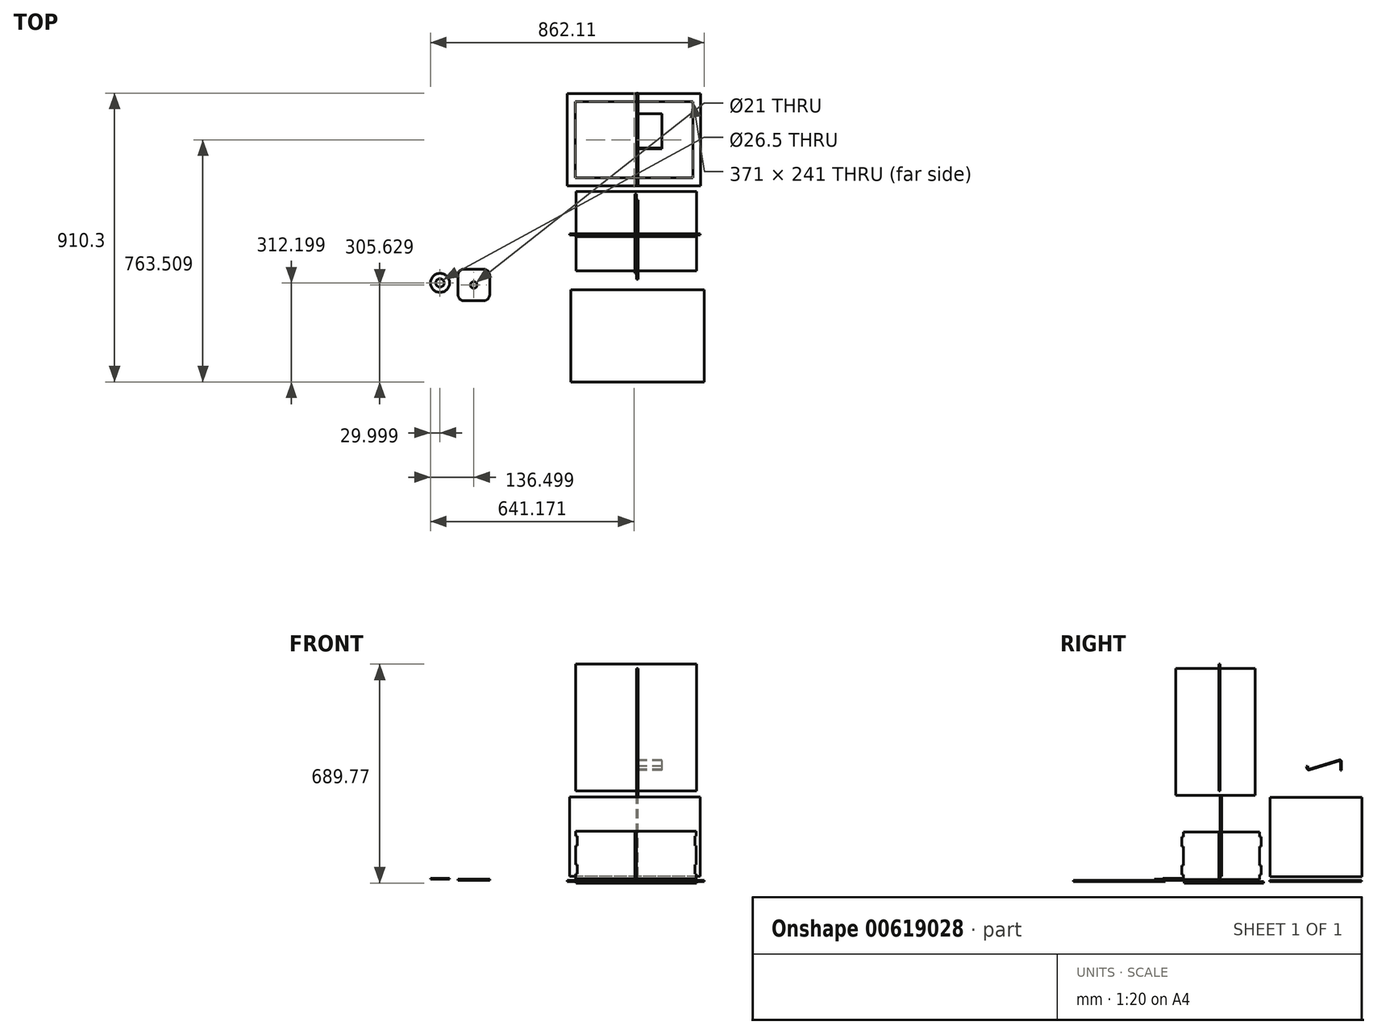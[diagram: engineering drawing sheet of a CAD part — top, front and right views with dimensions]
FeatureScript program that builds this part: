
annotation { "Feature Type Name" : "Feature", "Feature Type Description" : "" }
export const myFeature = defineFeature(function(context is Context, id is Id, definition is map)
    precondition{}
    {
        {
            var Q0;
            Q0=qCreatedBy(makeId("Top.planeOp"),FACE);
            var sketch = newSketch(context, id + "F0", { "sketchPlane" : qUnion([Q0])});
            skLineSegment(sketch, "E0.bottom", {"start": v(-185.88, 137.35) * mm, "end": v(194.12, 137.35) * mm});
            skLineSegment(sketch, "E0.top", {"start": v(-185.88, -112.65) * mm, "end": v(194.12, -112.65) * mm});
            skLineSegment(sketch, "E0.left", {"start": v(-185.88, 137.35) * mm, "end": v(-185.88, -112.65) * mm});
            skLineSegment(sketch, "E0.right", {"start": v(194.12, 137.35) * mm, "end": v(194.12, -112.65) * mm});
            skSolve(sketch);
        }
        {
            var Q0;
            Q0 = qSketchRegion(id + "F0", true);
            extrude(context, id + "F1", {"entities" : qUnion([Q0]), "depth" : 4.5 * mm, "offsetDistance" : 25 * mm});
        }
        {
            var Q0;
            Q0=qCreatedBy(makeId("Front.planeOp"),FACE);
            var sketch = newSketch(context, id + "F2", { "sketchPlane" : qUnion([Q0])});
            skLineSegment(sketch, "E1.bottom", {"start": v(-187.27, 13.24) * mm, "end": v(192.73, 13.24) * mm});
            skLineSegment(sketch, "E1.top", {"start": v(-187.27, 163.24) * mm, "end": v(192.73, 163.24) * mm});
            skLineSegment(sketch, "E1.left", {"start": v(-187.27, 13.24) * mm, "end": v(-187.27, 28.24) * mm});
            skLineSegment(sketch, "E1.right", {"start": v(192.73, 13.24) * mm, "end": v(192.73, 28.24) * mm});
            skLineSegment(sketch, "E2", {"start": v(-187.27, 148.24) * mm, "end": v(-182.77, 148.24) * mm});
            skLineSegment(sketch, "E3", {"start": v(-182.77, 148.24) * mm, "end": v(-182.77, 118.24) * mm});
            skLineSegment(sketch, "E4", {"start": v(-182.77, 118.24) * mm, "end": v(-187.27, 118.24) * mm});
            skLineSegment(sketch, "E5", {"start": v(-187.27, 58.24) * mm, "end": v(-182.77, 58.24) * mm});
            skLineSegment(sketch, "E6", {"start": v(-182.77, 58.24) * mm, "end": v(-182.77, 28.24) * mm});
            skLineSegment(sketch, "E7", {"start": v(-182.77, 28.24) * mm, "end": v(-187.27, 28.24) * mm});
            skLineSegment(sketch, "E8.trimOffspring", {"start": v(-187.27, 148.24) * mm, "end": v(-187.27, 163.24) * mm});
            skLineSegment(sketch, "E9.trimOffspring", {"start": v(-187.27, 58.24) * mm, "end": v(-187.27, 118.24) * mm});
            skLineSegment(sketch, "E10", {"start": v(192.73, 148.24) * mm, "end": v(188.23, 148.24) * mm});
            skLineSegment(sketch, "E11", {"start": v(188.23, 148.24) * mm, "end": v(188.23, 118.24) * mm});
            skLineSegment(sketch, "E12", {"start": v(188.23, 118.24) * mm, "end": v(192.73, 118.24) * mm});
            skLineSegment(sketch, "E13", {"start": v(192.73, 58.24) * mm, "end": v(188.23, 58.24) * mm});
            skLineSegment(sketch, "E14", {"start": v(188.23, 58.24) * mm, "end": v(188.23, 28.24) * mm});
            skLineSegment(sketch, "E15", {"start": v(188.23, 28.24) * mm, "end": v(192.73, 28.24) * mm});
            skLineSegment(sketch, "E16.trimOffspring", {"start": v(192.73, 148.24) * mm, "end": v(192.73, 163.24) * mm});
            skLineSegment(sketch, "E17.trimOffspring", {"start": v(192.73, 58.24) * mm, "end": v(192.73, 118.24) * mm});
            skSolve(sketch);
        }
        {
            var Q0;
            Q0 = qSketchRegion(id + "F2", true);
            extrude(context, id + "F3", {"entities" : qUnion([Q0]), "depth" : 4.5 * mm, "offsetDistance" : 25 * mm});
        }
        {
            var Q0;
            Q0=qCreatedBy(makeId("Right.planeOp"),FACE);
            var sketch = newSketch(context, id + "F4", { "sketchPlane" : qUnion([Q0])});
            skLineSegment(sketch, "E18.bottom", {"start": v(-116.2, 10.64) * mm, "end": v(124.8, 10.64) * mm});
            skLineSegment(sketch, "E18.top", {"start": v(-116.2, 160.64) * mm, "end": v(124.8, 160.64) * mm});
            skLineSegment(sketch, "E18.left", {"start": v(-116.2, 10.64) * mm, "end": v(-116.2, 25.64) * mm});
            skLineSegment(sketch, "E18.right", {"start": v(124.8, 10.64) * mm, "end": v(124.8, 25.64) * mm});
            skLineSegment(sketch, "E19", {"start": v(-116.2, 145.64) * mm, "end": v(-120.7, 145.64) * mm});
            skLineSegment(sketch, "E20", {"start": v(-120.7, 145.64) * mm, "end": v(-120.7, 115.64) * mm});
            skLineSegment(sketch, "E21", {"start": v(-120.7, 115.64) * mm, "end": v(-116.2, 115.64) * mm});
            skLineSegment(sketch, "E22", {"start": v(-116.2, 55.64) * mm, "end": v(-120.7, 55.64) * mm});
            skLineSegment(sketch, "E23", {"start": v(-120.7, 55.64) * mm, "end": v(-120.7, 25.64) * mm});
            skLineSegment(sketch, "E24", {"start": v(-120.7, 25.64) * mm, "end": v(-116.2, 25.64) * mm});
            skLineSegment(sketch, "E25.trimOffspring", {"start": v(-116.2, 145.64) * mm, "end": v(-116.2, 160.64) * mm});
            skLineSegment(sketch, "E26.trimOffspring", {"start": v(-116.2, 55.64) * mm, "end": v(-116.2, 115.64) * mm});
            skLineSegment(sketch, "E27", {"start": v(124.8, 145.64) * mm, "end": v(129.3, 145.64) * mm});
            skLineSegment(sketch, "E28", {"start": v(129.3, 145.64) * mm, "end": v(129.3, 115.64) * mm});
            skLineSegment(sketch, "E29", {"start": v(129.3, 115.64) * mm, "end": v(124.8, 115.64) * mm});
            skLineSegment(sketch, "E30", {"start": v(124.8, 55.64) * mm, "end": v(129.3, 55.64) * mm});
            skLineSegment(sketch, "E31", {"start": v(129.3, 55.64) * mm, "end": v(129.3, 25.64) * mm});
            skLineSegment(sketch, "E32", {"start": v(129.3, 25.64) * mm, "end": v(124.8, 25.64) * mm});
            skLineSegment(sketch, "E33.trimOffspring", {"start": v(124.8, 145.64) * mm, "end": v(124.8, 160.64) * mm});
            skLineSegment(sketch, "E34.trimOffspring", {"start": v(124.8, 55.64) * mm, "end": v(124.8, 115.64) * mm});
            skSolve(sketch);
        }
        {
            var Q0;
            Q0 = qSketchRegion(id + "F4", true);
            extrude(context, id + "F5", {"entities" : qUnion([Q0]), "depth" : 4.5 * mm, "offsetDistance" : 25 * mm});
        }
        {
            var Q0;
            Q0=makeQuery(id+"F1.opExtrude","CAP_FACE",FACE,{"disambiguationData":[OSD([sQuery(id+"F0.wireOp",EDGE,"E0.bottom"),sQuery(id+"F0.wireOp",EDGE,"E0.top"),sQuery(id+"F0.wireOp",EDGE,"E0.left"),sQuery(id+"F0.wireOp",EDGE,"E0.right")])],"isStart":false});
            var sketch = newSketch(context, id + "F6", { "sketchPlane" : qUnion([Q0])});
            skLineSegment(sketch, "E35.bottom", {"start": v(-189.13, 179.9) * mm, "end": v(181.87, 179.9) * mm});
            skLineSegment(sketch, "E35.top", {"start": v(-189.13, 420.9) * mm, "end": v(181.87, 420.9) * mm});
            skLineSegment(sketch, "E35.left", {"start": v(-189.13, 179.9) * mm, "end": v(-189.13, 420.9) * mm});
            skLineSegment(sketch, "E35.right", {"start": v(181.87, 179.9) * mm, "end": v(181.87, 420.9) * mm});
            skLineSegment(sketch, "E36.bottom", {"start": v(-213.63, 155.4) * mm, "end": v(206.37, 155.4) * mm});
            skLineSegment(sketch, "E36.top", {"start": v(-213.63, 445.4) * mm, "end": v(206.37, 445.4) * mm});
            skLineSegment(sketch, "E36.left", {"start": v(-213.63, 155.4) * mm, "end": v(-213.63, 445.4) * mm});
            skLineSegment(sketch, "E36.right", {"start": v(206.37, 155.4) * mm, "end": v(206.37, 445.4) * mm});
            skSolve(sketch);
        }
        {
            var Q0;
            Q0 = qSketchRegion(id + "F6", true);
            extrude(context, id + "F7", {"entities" : qUnion([Q0]), "depth" : 4.5 * mm, "offsetDistance" : 25 * mm});
        }
        {
            var Q0;
            Q0=makeQuery(id+"F5.opExtrude","CAP_FACE",FACE,{"disambiguationData":[OSD([sQuery(id+"F4.wireOp",EDGE,"E18.bottom"),sQuery(id+"F4.wireOp",EDGE,"E18.top"),sQuery(id+"F4.wireOp",EDGE,"E18.left"),sQuery(id+"F4.wireOp",EDGE,"E18.right"),sQuery(id+"F4.wireOp",EDGE,"E19"),sQuery(id+"F4.wireOp",EDGE,"E20"),sQuery(id+"F4.wireOp",EDGE,"E21"),sQuery(id+"F4.wireOp",EDGE,"E22"),sQuery(id+"F4.wireOp",EDGE,"E23"),sQuery(id+"F4.wireOp",EDGE,"E24"),sQuery(id+"F4.wireOp",EDGE,"E25.trimOffspring"),sQuery(id+"F4.wireOp",EDGE,"E26.trimOffspring"),sQuery(id+"F4.wireOp",EDGE,"E27"),sQuery(id+"F4.wireOp",EDGE,"E28"),sQuery(id+"F4.wireOp",EDGE,"E29"),sQuery(id+"F4.wireOp",EDGE,"E30"),sQuery(id+"F4.wireOp",EDGE,"E31"),sQuery(id+"F4.wireOp",EDGE,"E32"),sQuery(id+"F4.wireOp",EDGE,"E33.trimOffspring"),sQuery(id+"F4.wireOp",EDGE,"E34.trimOffspring")])],"isStart":false});
            var sketch = newSketch(context, id + "F8", { "sketchPlane" : qUnion([Q0])});
            skLineSegment(sketch, "E37.bottom", {"start": v(157.19, 19.82) * mm, "end": v(447.19, 19.82) * mm});
            skLineSegment(sketch, "E37.top", {"start": v(157.19, 269.82) * mm, "end": v(447.19, 269.82) * mm});
            skLineSegment(sketch, "E37.left", {"start": v(157.19, 19.82) * mm, "end": v(157.19, 269.82) * mm});
            skLineSegment(sketch, "E37.right", {"start": v(447.19, 19.82) * mm, "end": v(447.19, 269.82) * mm});
            skSolve(sketch);
        }
        {
            var Q0;
            Q0 = qSketchRegion(id + "F8", true);
            extrude(context, id + "F9", {"entities" : qUnion([Q0]), "depth" : 4.5 * mm, "offsetDistance" : 25 * mm});
        }
        {
            var Q0;
            Q0=makeQuery(id+"F3.opExtrude","CAP_FACE",FACE,{"disambiguationData":[OSD([sQuery(id+"F2.wireOp",EDGE,"E1.bottom"),sQuery(id+"F2.wireOp",EDGE,"E1.top"),sQuery(id+"F2.wireOp",EDGE,"E1.left"),sQuery(id+"F2.wireOp",EDGE,"E1.right"),sQuery(id+"F2.wireOp",EDGE,"E2"),sQuery(id+"F2.wireOp",EDGE,"E3"),sQuery(id+"F2.wireOp",EDGE,"E4"),sQuery(id+"F2.wireOp",EDGE,"E5"),sQuery(id+"F2.wireOp",EDGE,"E6"),sQuery(id+"F2.wireOp",EDGE,"E7"),sQuery(id+"F2.wireOp",EDGE,"E8.trimOffspring"),sQuery(id+"F2.wireOp",EDGE,"E9.trimOffspring"),sQuery(id+"F2.wireOp",EDGE,"E10"),sQuery(id+"F2.wireOp",EDGE,"E11"),sQuery(id+"F2.wireOp",EDGE,"E12"),sQuery(id+"F2.wireOp",EDGE,"E13"),sQuery(id+"F2.wireOp",EDGE,"E14"),sQuery(id+"F2.wireOp",EDGE,"E15"),sQuery(id+"F2.wireOp",EDGE,"E16.trimOffspring"),sQuery(id+"F2.wireOp",EDGE,"E17.trimOffspring")])],"isStart":true});
            var sketch = newSketch(context, id + "F10", { "sketchPlane" : qUnion([Q0])});
            skPoint(sketch, "E38.firstSnap0", {"position": v(-192.73, 20.74) * mm});
            skLineSegment(sketch, "E38.bottom", {"start": v(-204.65, 20.74) * mm, "end": v(206.35, 20.74) * mm});
            skLineSegment(sketch, "E38.top", {"start": v(-204.65, 270.74) * mm, "end": v(206.35, 270.74) * mm});
            skLineSegment(sketch, "E38.left", {"start": v(-204.65, 20.74) * mm, "end": v(-204.65, 270.74) * mm});
            skLineSegment(sketch, "E38.right", {"start": v(206.35, 20.74) * mm, "end": v(206.35, 270.74) * mm});
            skSolve(sketch);
        }
        {
            var Q0;
            Q0 = qSketchRegion(id + "F10", true);
            extrude(context, id + "F11", {"entities" : qUnion([Q0]), "depth" : 4.5 * mm, "offsetDistance" : 25 * mm});
        }
        {
            var Q0;
            Q0=makeQuery(id+"F1.opExtrude","CAP_FACE",FACE,{"disambiguationData":[OSD([sQuery(id+"F0.wireOp",EDGE,"E0.bottom"),sQuery(id+"F0.wireOp",EDGE,"E0.top"),sQuery(id+"F0.wireOp",EDGE,"E0.left"),sQuery(id+"F0.wireOp",EDGE,"E0.right")])],"isStart":false});
            var sketch = newSketch(context, id + "F12", { "sketchPlane" : qUnion([Q0])});
            skLineSegment(sketch, "E39.bottom", {"start": v(-202.69, -463.1) * mm, "end": v(217.31, -463.1) * mm});
            skLineSegment(sketch, "E39.top", {"start": v(-202.69, -173.1) * mm, "end": v(217.31, -173.1) * mm});
            skLineSegment(sketch, "E39.left", {"start": v(-202.69, -463.1) * mm, "end": v(-202.69, -173.1) * mm});
            skLineSegment(sketch, "E39.right", {"start": v(217.31, -463.1) * mm, "end": v(217.31, -173.1) * mm});
            skSolve(sketch);
        }
        {
            var Q0;
            Q0 = qSketchRegion(id + "F12", true);
            extrude(context, id + "F13", {"entities" : qUnion([Q0]), "depth" : 4.5 * mm, "offsetDistance" : 25 * mm});
        }
        {
            var Q0;
            Q0=makeQuery(id+"F11.opExtrude","CAP_FACE",FACE,{"disambiguationData":[OSD([sQuery(id+"F10.wireOp",EDGE,"E38.bottom"),sQuery(id+"F10.wireOp",EDGE,"E38.top"),sQuery(id+"F10.wireOp",EDGE,"E38.left"),sQuery(id+"F10.wireOp",EDGE,"E38.right")])],"isStart":true});
            var sketch = newSketch(context, id + "F14", { "sketchPlane" : qUnion([Q0])});
            skLineSegment(sketch, "E40.bottom", {"start": v(-186.9, 289.77) * mm, "end": v(193.1, 289.77) * mm});
            skLineSegment(sketch, "E40.top", {"start": v(-186.9, 689.77) * mm, "end": v(193.1, 689.77) * mm});
            skLineSegment(sketch, "E40.left", {"start": v(-186.9, 289.77) * mm, "end": v(-186.9, 689.77) * mm});
            skLineSegment(sketch, "E40.right", {"start": v(193.1, 289.77) * mm, "end": v(193.1, 689.77) * mm});
            skSolve(sketch);
        }
        {
            var Q0;
            Q0 = qSketchRegion(id + "F14", true);
            extrude(context, id + "F15", {"entities" : qUnion([Q0]), "depth" : 4.5 * mm, "offsetDistance" : 25 * mm});
        }
        {
            var Q0;
            Q0=makeQuery(id+"F5.opExtrude","CAP_FACE",FACE,{"disambiguationData":[OSD([sQuery(id+"F4.wireOp",EDGE,"E18.bottom"),sQuery(id+"F4.wireOp",EDGE,"E18.top"),sQuery(id+"F4.wireOp",EDGE,"E18.left"),sQuery(id+"F4.wireOp",EDGE,"E18.right"),sQuery(id+"F4.wireOp",EDGE,"E19"),sQuery(id+"F4.wireOp",EDGE,"E20"),sQuery(id+"F4.wireOp",EDGE,"E21"),sQuery(id+"F4.wireOp",EDGE,"E22"),sQuery(id+"F4.wireOp",EDGE,"E23"),sQuery(id+"F4.wireOp",EDGE,"E24"),sQuery(id+"F4.wireOp",EDGE,"E25.trimOffspring"),sQuery(id+"F4.wireOp",EDGE,"E26.trimOffspring"),sQuery(id+"F4.wireOp",EDGE,"E27"),sQuery(id+"F4.wireOp",EDGE,"E28"),sQuery(id+"F4.wireOp",EDGE,"E29"),sQuery(id+"F4.wireOp",EDGE,"E30"),sQuery(id+"F4.wireOp",EDGE,"E31"),sQuery(id+"F4.wireOp",EDGE,"E32"),sQuery(id+"F4.wireOp",EDGE,"E33.trimOffspring"),sQuery(id+"F4.wireOp",EDGE,"E34.trimOffspring")])],"isStart":false});
            var sketch = newSketch(context, id + "F16", { "sketchPlane" : qUnion([Q0])});
            skLineSegment(sketch, "E41.bottom", {"start": v(-140.06, 276.07) * mm, "end": v(109.94, 276.07) * mm});
            skLineSegment(sketch, "E41.top", {"start": v(-140.06, 676.07) * mm, "end": v(109.94, 676.07) * mm});
            skLineSegment(sketch, "E41.left", {"start": v(-140.06, 276.07) * mm, "end": v(-140.06, 676.07) * mm});
            skLineSegment(sketch, "E41.right", {"start": v(109.94, 276.07) * mm, "end": v(109.94, 676.07) * mm});
            skSolve(sketch);
        }
        {
            var Q0;
            Q0 = qSketchRegion(id + "F16", true);
            extrude(context, id + "F17", {"entities" : qUnion([Q0]), "depth" : 4.5 * mm, "offsetDistance" : 25 * mm});
        }
        {
            var Q0;
            Q0=makeQuery(id+"F9.opExtrude","CAP_FACE",FACE,{"disambiguationData":[OSD([sQuery(id+"F8.wireOp",EDGE,"E37.bottom"),sQuery(id+"F8.wireOp",EDGE,"E37.top"),sQuery(id+"F8.wireOp",EDGE,"E37.left"),sQuery(id+"F8.wireOp",EDGE,"E37.right")])],"isStart":false});
            var sketch = newSketch(context, id + "F18", { "sketchPlane" : qUnion([Q0])});
            skLineSegment(sketch, "E42", {"start": v(382.2, 354.76) * mm, "end": v(379.2, 354.76) * mm});
            skLineSegment(sketch, "E43", {"start": v(379.2, 354.76) * mm, "end": v(379.2, 383.04) * mm});
            skLineSegment(sketch, "E44", {"start": v(376.63, 384.96) * mm, "end": v(280.83, 356.29) * mm});
            skLineSegment(sketch, "E45", {"start": v(277.48, 360.5) * mm, "end": v(274.9, 369.16) * mm});
            skLineSegment(sketch, "E46", {"start": v(274.9, 369.16) * mm, "end": v(272.02, 368.3) * mm});
            skLineSegment(sketch, "E47", {"start": v(272.02, 368.3) * mm, "end": v(274.6, 359.64) * mm});
            skPoint(sketch, "E48.visualSharp", {"position": v(276.04, 354.85) * mm});
            skArc(sketch, "E48.filletArc", {"start": v(274.6, 359.64) * mm, "mid": v(277.02, 356.68) * mm, "end": v(280.83, 356.29) * mm});
            skPoint(sketch, "E49.visualSharp", {"position": v(278.06, 358.59) * mm});
            skArc(sketch, "E49.filletArc", {"start": v(277.48, 360.5) * mm, "mid": v(278.45, 359.32) * mm, "end": v(279.97, 359.16) * mm});
            skPoint(sketch, "E50.visualSharp", {"position": v(379.2, 385.73) * mm});
            skArc(sketch, "E50.filletArc", {"start": v(379.2, 383.04) * mm, "mid": v(378.4, 384.65) * mm, "end": v(376.63, 384.96) * mm});
            skPoint(sketch, "E51.visualSharp", {"position": v(382.2, 389.76) * mm});
            skLineSegment(sketch, "E52", {"start": v(382.2, 354.76) * mm, "end": v(382.2, 383.04) * mm});
            skLineSegment(sketch, "E53", {"start": v(279.97, 359.16) * mm, "end": v(375.77, 387.83) * mm});
            skArc(sketch, "E54", {"start": v(382.2, 383.04) * mm, "mid": v(380.2, 387.05) * mm, "end": v(375.77, 387.83) * mm});
            skSolve(sketch);
        }
        {
            var Q0;
            Q0 = qSketchRegion(id + "F18", true);
            extrude(context, id + "F19", {"entities" : qUnion([Q0]), "depth" : 75 * mm, "offsetDistance" : 25 * mm});
        }
        {
            var Q0;
            Q0=makeQuery(id+"F13.opExtrude","CAP_FACE",FACE,{"disambiguationData":[OSD([sQuery(id+"F12.wireOp",EDGE,"E39.bottom"),sQuery(id+"F12.wireOp",EDGE,"E39.top"),sQuery(id+"F12.wireOp",EDGE,"E39.left"),sQuery(id+"F12.wireOp",EDGE,"E39.right")])],"isStart":false});
            var sketch = newSketch(context, id + "F20", { "sketchPlane" : qUnion([Q0])});
            skCircle(sketch, "E55", {"center": v(-508.3, -157.48) * mm, "radius": 10.5 * mm});
            skLineSegment(sketch, "E56.bottom", {"start": v(-478.3, -207.48) * mm, "end": v(-538.3, -207.48) * mm});
            skLineSegment(sketch, "E56.top", {"start": v(-478.3, -107.48) * mm, "end": v(-538.3, -107.48) * mm});
            skLineSegment(sketch, "E56.left", {"start": v(-458.3, -187.48) * mm, "end": v(-458.3, -127.48) * mm});
            skLineSegment(sketch, "E56.right", {"start": v(-558.3, -187.48) * mm, "end": v(-558.3, -127.48) * mm});
            skPoint(sketch, "E57.visualSharp", {"position": v(-558.3, -107.48) * mm});
            skArc(sketch, "E57.filletArc", {"start": v(-538.3, -107.48) * mm, "mid": v(-552.44, -113.34) * mm, "end": v(-558.3, -127.48) * mm});
            skPoint(sketch, "E58.visualSharp", {"position": v(-558.3, -207.48) * mm});
            skArc(sketch, "E58.filletArc", {"start": v(-558.3, -187.48) * mm, "mid": v(-552.44, -201.62) * mm, "end": v(-538.3, -207.48) * mm});
            skPoint(sketch, "E59.visualSharp", {"position": v(-458.3, -207.48) * mm});
            skArc(sketch, "E59.filletArc", {"start": v(-478.3, -207.48) * mm, "mid": v(-464.16, -201.62) * mm, "end": v(-458.3, -187.48) * mm});
            skPoint(sketch, "E60.visualSharp", {"position": v(-458.3, -107.48) * mm});
            skArc(sketch, "E60.filletArc", {"start": v(-458.3, -127.48) * mm, "mid": v(-464.16, -113.34) * mm, "end": v(-478.3, -107.48) * mm});
            skPoint(sketch, "E61.start.orphan", {"position": v(-508.3, -107.48) * mm});
            skPoint(sketch, "E62.trimOffspring.end.orphan", {"position": v(-508.3, -207.48) * mm});
            skSolve(sketch);
        }
        {
            var Q0;
            Q0 = qSketchRegion(id + "F20", true);
            extrude(context, id + "F21", {"entities" : qUnion([Q0]), "depth" : 3 * mm, "offsetDistance" : 25 * mm});
        }
        {
            var Q0;
            Q0=makeQuery(id+"F21.opExtrude","CAP_FACE",FACE,{"disambiguationData":[OSD([sQuery(id+"F20.wireOp",EDGE,"E55"),sQuery(id+"F20.wireOp",EDGE,"E56.bottom"),sQuery(id+"F20.wireOp",EDGE,"E56.top"),sQuery(id+"F20.wireOp",EDGE,"E56.left"),sQuery(id+"F20.wireOp",EDGE,"E56.right"),sQuery(id+"F20.wireOp",EDGE,"E57.filletArc"),sQuery(id+"F20.wireOp",EDGE,"E58.filletArc"),sQuery(id+"F20.wireOp",EDGE,"E59.filletArc"),sQuery(id+"F20.wireOp",EDGE,"E60.filletArc")])],"isStart":false});
            var sketch = newSketch(context, id + "F22", { "sketchPlane" : qUnion([Q0])});
            skCircle(sketch, "E63", {"center": v(-614.8, -150.91) * mm, "radius": 13.25 * mm});
            skCircle(sketch, "E64", {"center": v(-614.8, -150.91) * mm, "radius": 30 * mm});
            skSolve(sketch);
        }
        {
            var Q0;
            Q0=makeQuery(id+"F22.imprint","IMPRINT",FACE,{"disambiguationData":[TD([[makeQuery(id+"F22.imprint","IMPRINT",EDGE,{"derivedFrom":sQuery(id+"F22.wireOp",EDGE,"E63")}),-1.0]])]});
            var Q1;
            Q1 = qSketchRegion(id + "F22", true);
            extrude(context, id + "F23", {"entities" : qUnion([Q0, Q1]), "depth" : 3 * mm, "offsetDistance" : 25 * mm});
        }
    });
